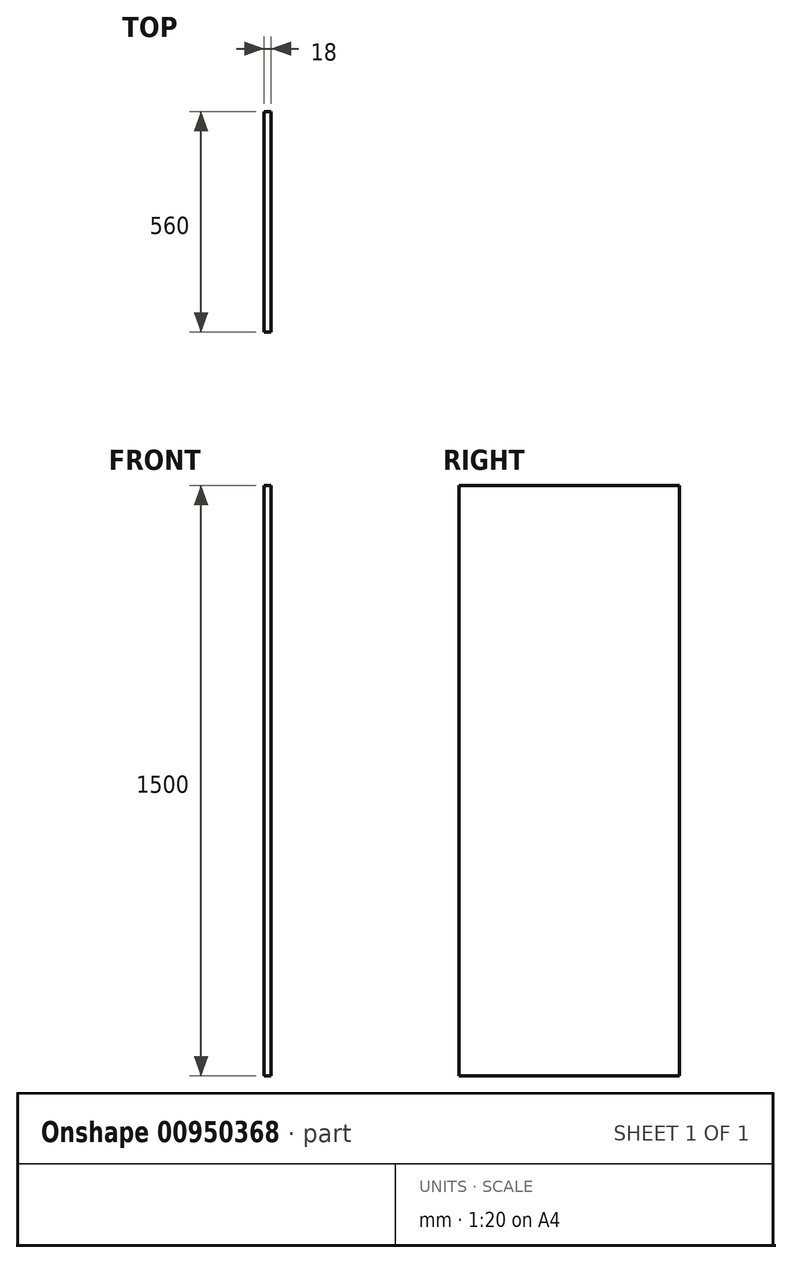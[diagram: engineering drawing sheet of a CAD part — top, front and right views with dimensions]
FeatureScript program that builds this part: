
annotation { "Feature Type Name" : "Feature", "Feature Type Description" : "" }
export const myFeature = defineFeature(function(context is Context, id is Id, definition is map)
    precondition{}
    {
        {
            var Q0;
            Q0=qCreatedBy(makeId("Right.planeOp"),FACE);
            var sketch = newSketch(context, id + "F0", { "sketchPlane" : qUnion([Q0])});
            skLineSegment(sketch, "E0.bottom", {"start": v(0, 1500) * mm, "end": v(560, 1500) * mm});
            skLineSegment(sketch, "E0.top", {"start": v(0, 0) * mm, "end": v(560, 0) * mm});
            skLineSegment(sketch, "E0.left", {"start": v(0, 1500) * mm, "end": v(0, 0) * mm});
            skLineSegment(sketch, "E0.right", {"start": v(560, 1500) * mm, "end": v(560, 0) * mm});
            skSolve(sketch);
        }
        {
            var Q0;
            Q0=makeQuery(id+"F0.imprint","IMPRINT",FACE,{"disambiguationData":[TD([[makeQuery(id+"F0.imprint","IMPRINT",EDGE,{"derivedFrom":sQuery(id+"F0.wireOp",EDGE,"E0.bottom")}),-1.0]])]});
            extrude(context, id + "F1", {"entities" : qUnion([Q0]), "depth" : 18 * mm, "offsetDistance" : 25 * mm});
        }
    });
